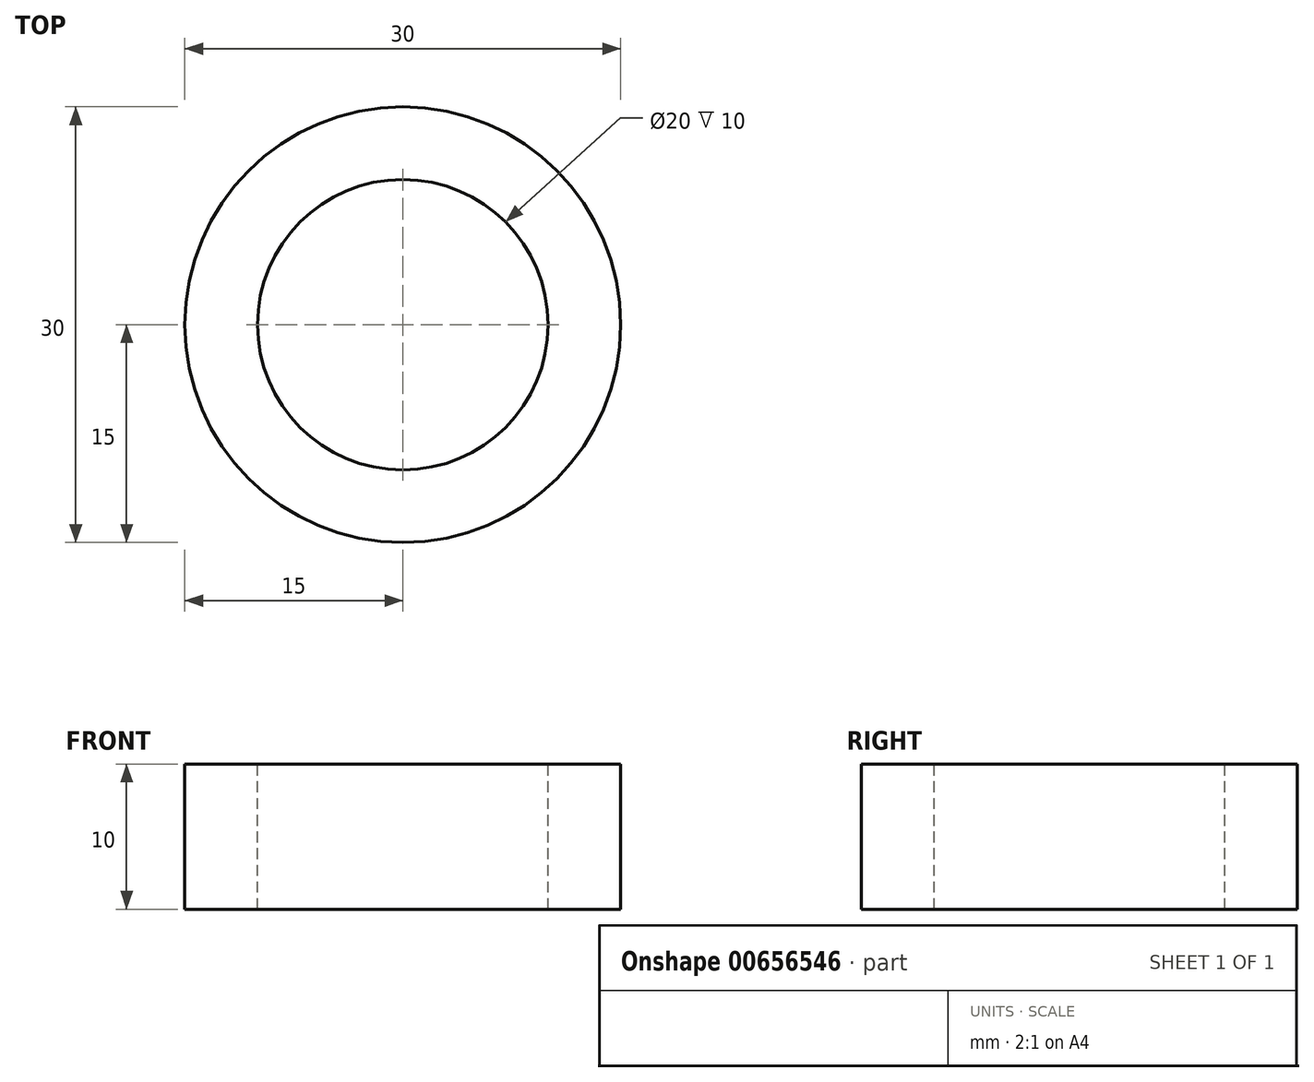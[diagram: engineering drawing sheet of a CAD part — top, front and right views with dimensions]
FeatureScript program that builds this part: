
annotation { "Feature Type Name" : "Feature", "Feature Type Description" : "" }
export const myFeature = defineFeature(function(context is Context, id is Id, definition is map)
    precondition{}
    {
        {
            var Q0;
            Q0=qCreatedBy(makeId("Top.planeOp"),FACE);
            var sketch = newSketch(context, id + "F0", { "sketchPlane" : qUnion([Q0])});
            skCircle(sketch, "E0", {"center": v(0, 0) * mm, "radius": 10 * mm});
            skCircle(sketch, "E1", {"center": v(0, 0) * mm, "radius": 15 * mm});
            skSolve(sketch);
        }
        {
            var Q0;
            Q0=makeQuery(id+"F0.imprint","IMPRINT",FACE,{"disambiguationData":[TD([[makeQuery(id+"F0.imprint","IMPRINT",EDGE,{"derivedFrom":sQuery(id+"F0.wireOp",EDGE,"E0")}),-1.0]])]});
            extrude(context, id + "F1", {"entities" : qUnion([Q0]), "oppositeDirection" : true, "depth" : 10 * mm, "offsetDistance" : 25 * mm});
        }
    });
